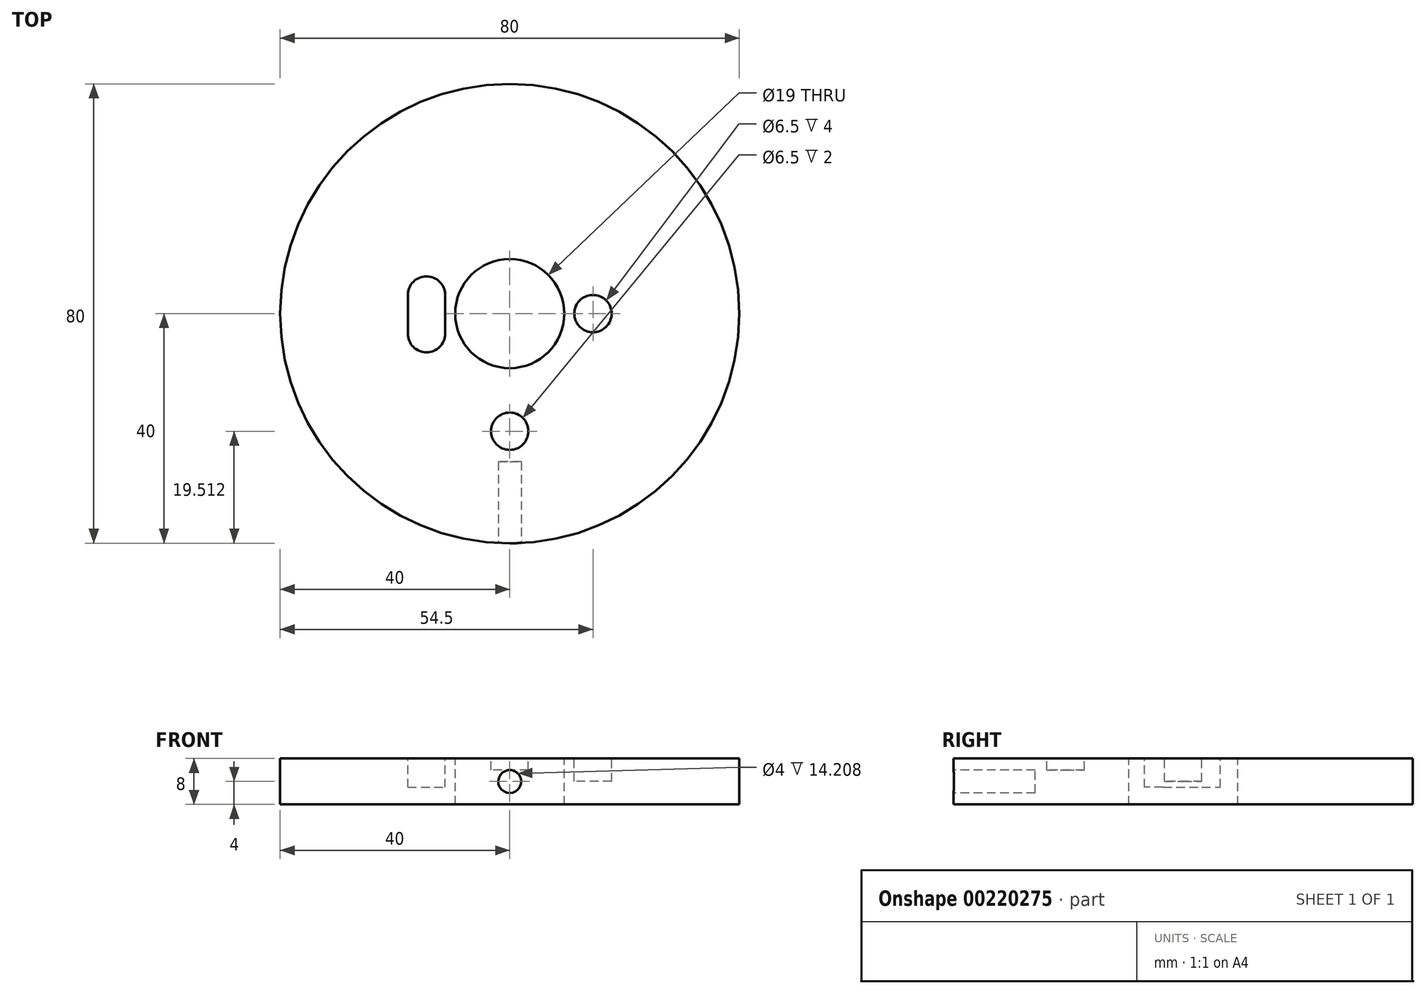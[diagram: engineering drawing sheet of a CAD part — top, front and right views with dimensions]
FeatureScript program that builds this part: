
annotation { "Feature Type Name" : "Feature", "Feature Type Description" : "" }
export const myFeature = defineFeature(function(context is Context, id is Id, definition is map)
    precondition{}
    {
        {
            var Q0;
            Q0=qCreatedBy(makeId("Top.planeOp"),FACE);
            var sketch = newSketch(context, id + "F0", { "sketchPlane" : qUnion([Q0])});
            skCircle(sketch, "E0", {"center": v(0, 0) * mm, "radius": 40 * mm});
            skSolve(sketch);
        }
        {
            var Q0;
            Q0 = qSketchRegion(id + "F0", true);
            extrude(context, id + "F1", {"entities" : qUnion([Q0]), "depth" : 8 * mm});
        }
        {
            var Q0;
            Q0=makeQuery(id+"F1.opExtrude","CAP_FACE",FACE,{"disambiguationData":[OSD([sQuery(id+"F0.wireOp",EDGE,"E0")])],"isStart":false});
            var sketch = newSketch(context, id + "F2", { "sketchPlane" : qUnion([Q0])});
            skCircle(sketch, "E1", {"center": v(0, 0) * mm, "radius": 9.5 * mm});
            skSolve(sketch);
        }
        {
            var Q0;
            Q0=makeQuery(id+"F2.imprint","IMPRINT",FACE,{"disambiguationData":[TD([[makeQuery(id+"F2.imprint","IMPRINT",EDGE,{"derivedFrom":sQuery(id+"F2.wireOp",EDGE,"E1")}),1.0]])]});
            var Q1;
            Q1=sQuery(id+"F2.wireOp",EDGE,"E1");
            extrude(context, id + "F3", {"entities" : qUnion([Q0]), "operationType" : NewBodyOperationType.REMOVE, "surfaceEntities" : qUnion([Q1]), "endBound" : BoundingType.THROUGH_ALL, "oppositeDirection" : true, "depth" : 25 * mm});
        }
        {
            var Q0;
            Q0=makeQuery(id+"F1.opExtrude","CAP_FACE",FACE,{"disambiguationData":[OSD([sQuery(id+"F0.wireOp",EDGE,"E0")])],"isStart":false});
            var sketch = newSketch(context, id + "F4", { "sketchPlane" : qUnion([Q0])});
            skPoint(sketch, "E2", {"position": v(14.5, 0) * mm});
            skPoint(sketch, "E3", {"position": v(0, -20.49) * mm});
            skPoint(sketch, "E4.MirrorP", {"position": v(-14.5, 0) * mm});
            skSolve(sketch);
        }
        {
            var Q0;
            Q0=makeQuery(id+"F4.imprint","IMPRINT",FACE,{"disambiguationData":[TD([[makeQuery(id+"F4.imprint","IMPRINT",EDGE,{"derivedFrom":makeQuery(id+"F1.opExtrude","CAP_EDGE",EDGE,{"disambiguationData":[OSD([sQuery(id+"F0.wireOp",EDGE,"E0")])],"isStart":false})}),1.0]])]});
            var sketch = newSketch(context, id + "F5", { "sketchPlane" : qUnion([Q0])});
            skCircle(sketch, "E5", {"center": v(14.5, 0) * mm, "radius": 3.25 * mm});
            skSolve(sketch);
        }
        {
            var Q0;
            Q0 = qSketchRegion(id + "F5", true);
            var Q1;
            Q1=sQuery(id+"F5.wireOp",EDGE,"E5");
            extrude(context, id + "F6", {"entities" : qUnion([Q0]), "operationType" : NewBodyOperationType.REMOVE, "surfaceEntities" : qUnion([Q1]), "oppositeDirection" : true, "depth" : 4 * mm});
        }
        {
            var Q0;
            Q0=makeQuery(id+"F4.imprint","IMPRINT",FACE,{"disambiguationData":[TD([[makeQuery(id+"F4.imprint","IMPRINT",EDGE,{"derivedFrom":makeQuery(id+"F1.opExtrude","CAP_EDGE",EDGE,{"disambiguationData":[OSD([sQuery(id+"F0.wireOp",EDGE,"E0")])],"isStart":false})}),1.0]])]});
            var sketch = newSketch(context, id + "F7", { "sketchPlane" : qUnion([Q0])});
            skLineSegment(sketch, "E6", {"start": v(-17.75, -3.5) * mm, "end": v(-17.75, 3.25) * mm});
            skArc(sketch, "E7", {"start": v(-11.25, 3.25) * mm, "mid": v(-14.5, 6.5) * mm, "end": v(-17.75, 3.25) * mm});
            skLineSegment(sketch, "E8", {"start": v(-11.25, 3.25) * mm, "end": v(-11.25, -3.5) * mm});
            skArc(sketch, "E9", {"start": v(-17.75, -3.5) * mm, "mid": v(-14.5, -6.75) * mm, "end": v(-11.25, -3.5) * mm});
            skSolve(sketch);
        }
        {
            var Q0;
            Q0 = qSketchRegion(id + "F7", true);
            extrude(context, id + "F8", {"entities" : qUnion([Q0]), "operationType" : NewBodyOperationType.REMOVE, "oppositeDirection" : true, "depth" : 5 * mm});
        }
        {
            var Q0;
            Q0=makeQuery(id+"F4.imprint","IMPRINT",FACE,{"disambiguationData":[TD([[makeQuery(id+"F4.imprint","IMPRINT",EDGE,{"derivedFrom":makeQuery(id+"F1.opExtrude","CAP_EDGE",EDGE,{"disambiguationData":[OSD([sQuery(id+"F0.wireOp",EDGE,"E0")])],"isStart":false})}),1.0]])]});
            var sketch = newSketch(context, id + "F9", { "sketchPlane" : qUnion([Q0])});
            skCircle(sketch, "E10", {"center": v(0, -20.49) * mm, "radius": 3.25 * mm});
            skSolve(sketch);
        }
        {
            var Q0;
            Q0 = qSketchRegion(id + "F9", true);
            var Q1;
            Q1=sQuery(id+"F9.wireOp",EDGE,"E10");
            extrude(context, id + "F10", {"entities" : qUnion([Q0]), "operationType" : NewBodyOperationType.REMOVE, "surfaceEntities" : qUnion([Q1]), "oppositeDirection" : true, "depth" : 2 * mm});
        }
        {
            var Q0;
            Q0=qCreatedBy(makeId("Front.planeOp"),FACE);
            cPlane(context, id + "F11", {"entities" : qUnion([Q0]), "cplaneType" : CPlaneType.OFFSET, "offset" : 40.8 * mm, "width" : 150 * mm, "height" : 150 * mm});
        }
        {
            var Q0;
            Q0=qCreatedBy(id+"F11.planeOp",FACE);
            var sketch = newSketch(context, id + "F12", { "sketchPlane" : qUnion([Q0])});
            skCircle(sketch, "E11", {"center": v(0, 4) * mm, "radius": 2 * mm});
            skSolve(sketch);
        }
        {
            var Q0;
            Q0 = qSketchRegion(id + "F12", true);
            extrude(context, id + "F13", {"entities" : qUnion([Q0]), "operationType" : NewBodyOperationType.REMOVE, "oppositeDirection" : true, "depth" : 15 * mm});
        }
    });
